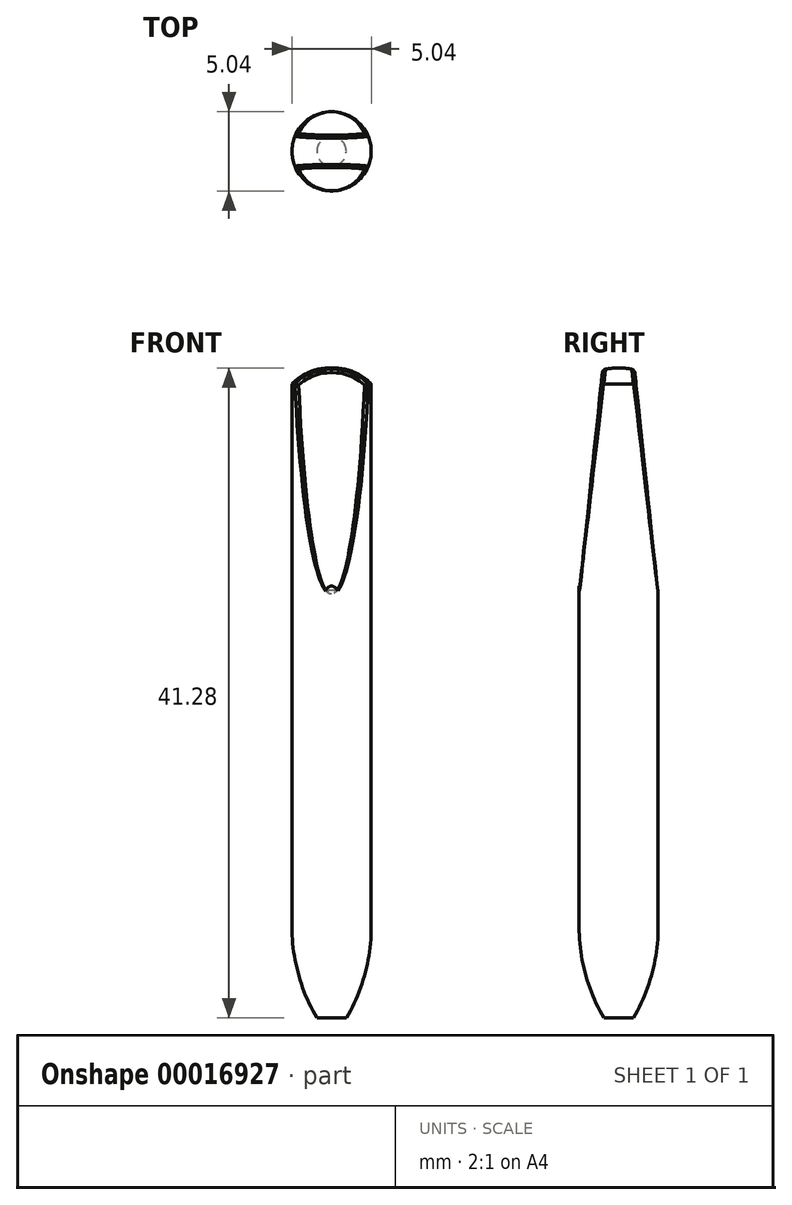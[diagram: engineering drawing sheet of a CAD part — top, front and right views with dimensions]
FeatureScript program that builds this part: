
annotation { "Feature Type Name" : "Feature", "Feature Type Description" : "" }
export const myFeature = defineFeature(function(context is Context, id is Id, definition is map)
    precondition{}
    {
        {
            var Q0;
            Q0=qCreatedBy(makeId("Top.planeOp"),FACE);
            var sketch = newSketch(context, id + "F0", { "sketchPlane" : qUnion([Q0])});
            skCircle(sketch, "E0", {"center": v(0, 0) * mm, "radius": 2.52 * mm});
            skSolve(sketch);
        }
        {
            var Q0;
            Q0 = qSketchRegion(id + "F0", true);
            extrude(context, id + "F1", {"entities" : qUnion([Q0]), "endBound" : BoundingType.SYMMETRIC, "depth" : 41.27 * mm});
        }
        {
            var Q0;
            Q0=qCreatedBy(makeId("Front.planeOp"),FACE);
            var sketch = newSketch(context, id + "F2", { "sketchPlane" : qUnion([Q0])});
            skArc(sketch, "E1", {"start": v(0.93, -20.64) * mm, "mid": v(2.11, -17.85) * mm, "end": v(2.52, -14.86) * mm});
            skLineSegment(sketch, "E2.0", {"start": v(0.93, -20.64) * mm, "end": v(2.52, -20.64) * mm});
            skLineSegment(sketch, "E3", {"start": v(2.52, -20.64) * mm, "end": v(2.52, -14.86) * mm});
            skPoint(sketch, "E4.orphan", {"position": v(-2.52, -20.64) * mm});
            skLineSegment(sketch, "E5.0", {"start": v(0.17, 20.64) * mm, "end": v(2.52, 20.64) * mm});
            skLineSegment(sketch, "E6", {"start": v(2.52, 20.64) * mm, "end": v(2.52, 19.64) * mm});
            skArc(sketch, "E7", {"start": v(2.51, 19.64) * mm, "mid": v(1.45, 20.38) * mm, "end": v(0.17, 20.64) * mm});
            skPoint(sketch, "E8.orphan", {"position": v(-2.52, 20.64) * mm});
            skSolve(sketch);
        }
        {
            var Q0;
            Q0 = qSketchRegion(id + "F2", true);
            var Q1;
            Q1=makeQuery(id+"F1.opExtrude","SWEPT_FACE",FACE,{"disambiguationData":[OSD([sQuery(id+"F0.wireOp",EDGE,"E0")])]});
            revolve(context, id + "F3", {"operationType" : NewBodyOperationType.REMOVE, "entities" : qUnion([Q0]), "axis" : qUnion([Q1]), "revolveType" : RevolveType.FULL, "oppositeDirection" : true});
        }
        {
            var Q0;
            Q0=makeQuery(id+"F1.opExtrude","CAP_FACE",FACE,{"disambiguationData":[OSD([sQuery(id+"F0.wireOp",EDGE,"E0")])],"isStart":false});
            var sketch = newSketch(context, id + "F4", { "sketchPlane" : qUnion([Q0])});
            skLineSegment(sketch, "E9.bottom", {"start": v(-5.56, 1) * mm, "end": v(6.68, 1) * mm});
            skLineSegment(sketch, "E9.top", {"start": v(-5.56, 4.65) * mm, "end": v(6.68, 4.65) * mm});
            skLineSegment(sketch, "E9.left", {"start": v(-5.56, 1) * mm, "end": v(-5.56, 4.65) * mm});
            skLineSegment(sketch, "E9.right", {"start": v(6.68, 1) * mm, "end": v(6.68, 4.65) * mm});
            skLineSegment(sketch, "E10.bottom", {"start": v(-5.17, -1) * mm, "end": v(5.88, -1) * mm});
            skLineSegment(sketch, "E10.top", {"start": v(-5.17, -3.97) * mm, "end": v(5.88, -3.97) * mm});
            skLineSegment(sketch, "E10.left", {"start": v(-5.17, -1) * mm, "end": v(-5.17, -3.97) * mm});
            skLineSegment(sketch, "E10.right", {"start": v(5.88, -1) * mm, "end": v(5.88, -3.97) * mm});
            skSolve(sketch);
        }
        {
            var Q0;
            Q0 = qSketchRegion(id + "F4", true);
            extrude(context, id + "F5", {"entities" : qUnion([Q0]), "operationType" : NewBodyOperationType.REMOVE, "endBound" : BoundingType.THROUGH_ALL, "oppositeDirection" : true, "depth" : 30 * mm, "hasDraft" : true, "draftAngle" : 6 * degree, "draftPullDirection" : true});
        }
        {
            var Q0;
            Q0=makeQuery(id+"F5.boolean.opBoolean","INTERSECT",EDGE,{"derivedFrom":[makeQuery(id+"F3.boolean.opBoolean","COPY",FACE,{"derivedFrom":makeQuery(id+"F3.opRevolve","SWEPT_FACE",FACE,{"disambiguationData":[OSD([sQuery(id+"F2.wireOp",EDGE,"E7")])]})}),makeQuery(id+"F5.opExtrude","SWEPT_FACE",FACE,{"disambiguationData":[OSD([sQuery(id+"F4.wireOp",EDGE,"E10.bottom")])]})]});
            var Q1;
            Q1=makeQuery(id+"F5.boolean.opBoolean","INTERSECT",EDGE,{"derivedFrom":[makeQuery(id+"F3.boolean.opBoolean","COPY",FACE,{"derivedFrom":makeQuery(id+"F3.opRevolve","SWEPT_FACE",FACE,{"disambiguationData":[OSD([sQuery(id+"F2.wireOp",EDGE,"E7")])]})}),makeQuery(id+"F5.opExtrude","SWEPT_FACE",FACE,{"disambiguationData":[OSD([sQuery(id+"F4.wireOp",EDGE,"E9.bottom")])]})]});
            var Q2;
            Q2=makeQuery(id+"F5.boolean.opBoolean","SPLIT",EDGE,{"disambiguationData":[OD(1.0)],"derivedFrom":makeQuery(id+"F3.boolean.opBoolean","COPY",EDGE,{"derivedFrom":makeQuery(id+"F3.opRevolve","SWEPT_EDGE",EDGE,{"disambiguationData":[OSD([sQuery(id+"F2.wireOp",EDGE,"E6"),sQuery(id+"F2.wireOp",EDGE,"E7")])]})})});
            var Q3;
            Q3=makeQuery(id+"F5.boolean.opBoolean","SPLIT",EDGE,{"disambiguationData":[OD(0.0)],"derivedFrom":makeQuery(id+"F3.boolean.opBoolean","COPY",EDGE,{"derivedFrom":makeQuery(id+"F3.opRevolve","SWEPT_EDGE",EDGE,{"disambiguationData":[OSD([sQuery(id+"F2.wireOp",EDGE,"E6"),sQuery(id+"F2.wireOp",EDGE,"E7")])]})})});
            var Q4;
            Q4=makeQuery(id+"F5.boolean.opBoolean","INTERSECT",EDGE,{"disambiguationData":[OD(1.0)],"derivedFrom":[makeQuery(id+"F1.opExtrude","SWEPT_FACE",FACE,{"disambiguationData":[OSD([sQuery(id+"F0.wireOp",EDGE,"E0")])]}),makeQuery(id+"F5.opExtrude","SWEPT_FACE",FACE,{"disambiguationData":[OSD([sQuery(id+"F4.wireOp",EDGE,"E10.bottom")])]})]});
            var Q5;
            Q5=makeQuery(id+"F5.boolean.opBoolean","INTERSECT",EDGE,{"disambiguationData":[OD(0.0)],"derivedFrom":[makeQuery(id+"F1.opExtrude","SWEPT_FACE",FACE,{"disambiguationData":[OSD([sQuery(id+"F0.wireOp",EDGE,"E0")])]}),makeQuery(id+"F5.opExtrude","SWEPT_FACE",FACE,{"disambiguationData":[OSD([sQuery(id+"F4.wireOp",EDGE,"E10.bottom")])]})]});
            var Q6;
            Q6=makeQuery(id+"F5.boolean.opBoolean","INTERSECT",EDGE,{"derivedFrom":[makeQuery(id+"F1.opExtrude","SWEPT_FACE",FACE,{"disambiguationData":[OSD([sQuery(id+"F0.wireOp",EDGE,"E0")])]}),makeQuery(id+"F5.opExtrude","SWEPT_FACE",FACE,{"disambiguationData":[OSD([sQuery(id+"F4.wireOp",EDGE,"E9.bottom")])]})]});
            fillet(context, id + "F6", {"entities" : qUnion([Q0, Q1, Q2, Q3, Q4, Q5, Q6]), "radius" : .25 * mm, "tangentPropagation" : true, "allowEdgeOverflow" : false});
        }
    });
